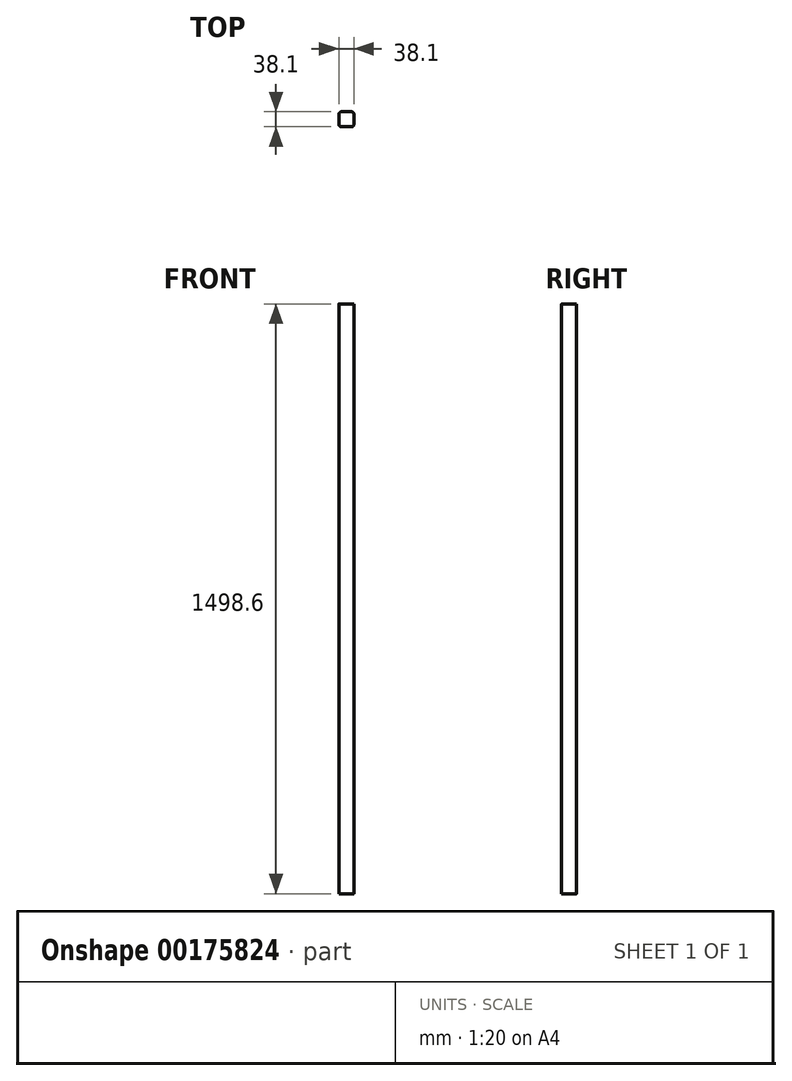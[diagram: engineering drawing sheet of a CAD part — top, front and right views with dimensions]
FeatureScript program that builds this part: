
annotation { "Feature Type Name" : "Feature", "Feature Type Description" : "" }
export const myFeature = defineFeature(function(context is Context, id is Id, definition is map)
    precondition{}
    {
        {
            var Q0;
            Q0=qCreatedBy(makeId("Top.planeOp"),FACE);
            var sketch = newSketch(context, id + "F0", { "sketchPlane" : qUnion([Q0])});
            skLineSegment(sketch, "E0.bottom", {"start": v(12.7, 19.05) * mm, "end": v(-12.7, 19.05) * mm});
            skLineSegment(sketch, "E0.top", {"start": v(12.7, -19.05) * mm, "end": v(-12.7, -19.05) * mm});
            skLineSegment(sketch, "E0.left", {"start": v(19.05, 12.7) * mm, "end": v(19.05, -12.7) * mm});
            skLineSegment(sketch, "E0.right", {"start": v(-19.05, 12.7) * mm, "end": v(-19.05, -12.7) * mm});
            skPoint(sketch, "E0.middle", {"position": v(0, 0) * mm});
            skPoint(sketch, "E1.visualSharp", {"position": v(-19.05, 19.05) * mm});
            skArc(sketch, "E1.filletArc", {"start": v(-12.7, 19.05) * mm, "mid": v(-17.2, 17.2) * mm, "end": v(-19.05, 12.7) * mm});
            skPoint(sketch, "E2.visualSharp", {"position": v(19.05, 19.05) * mm});
            skArc(sketch, "E2.filletArc", {"start": v(19.05, 12.7) * mm, "mid": v(17.2, 17.2) * mm, "end": v(12.7, 19.05) * mm});
            skPoint(sketch, "E3.visualSharp", {"position": v(19.05, -19.05) * mm});
            skArc(sketch, "E3.filletArc", {"start": v(12.7, -19.05) * mm, "mid": v(17.2, -17.2) * mm, "end": v(19.05, -12.7) * mm});
            skPoint(sketch, "E4.visualSharp", {"position": v(-19.05, -19.05) * mm});
            skArc(sketch, "E4.filletArc", {"start": v(-19.05, -12.7) * mm, "mid": v(-17.2, -17.2) * mm, "end": v(-12.7, -19.05) * mm});
            skSolve(sketch);
        }
        {
            var Q0;
            Q0=qSketchRegion(id+"F0",true);
            extrude(context, id + "F1", {"entities" : qUnion([Q0]), "depth" : 1498.6 * mm, "offsetDistance" : 25.4 * mm});
        }
    });
